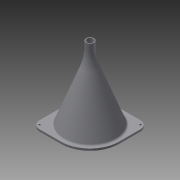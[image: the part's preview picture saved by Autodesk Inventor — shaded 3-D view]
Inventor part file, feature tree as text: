
AUTODESK INVENTOR PART (.ipt)
format: ipt  version: 2014 SP1 (Build 180222100, 222)  size: 177,152 bytes
history: native  units: in
note: dims shown in document units (in); Inventor stores cm internally (conversion verified against a paired STEP export)
features: sketch x5, extrude x4, other x1, plane x1, revolve x1
ambient origin geometry x8: Origin, YZ Plane, XZ Plane, XY Plane, X Axis, Y Axis, Z Axis, Center Point
bodies: Solid1 (feature_tree)
feature tree (12):
  extrude  "Extrusion1"  Depth=0.0787in
  extrude  "Extrusion2"  Depth=0.25in
  other  "Work Axis2"
  plane  "Work Plane5"
  revolve  "Revolution4"  [1 undecoded]
  extrude  "Extrusion6"  Depth=0.125in
  extrude  "Extrusion7"  TaperAngle=90.0deg  [1 undecoded]
  sketch  "Sketch1"  dims[d0=3.1496in d1=0.0787in]
  sketch  "Sketch2"  dims[d2=0.25in d3=0.0in d4=0.1969in]
  sketch  "Sketch10"  dims[d5=1.8505in d6=0.5in]
  sketch  "Sketch11"  dims[d7=0.125in d8=0.0in d40=0.125in]
  sketch  "Sketch12"  dims[d43=3.0in d53=90.0deg d54=90.0deg d59=1.25in d60=0.0741in d62=0.1165in d63=0.1165in d64=0.125in d65=0.0in d66=0.25in d67=0.0in]
note: 2 required parameter values undecoded (feature->parameter linkage not recoverable at this tier; creation-order binding heuristic only, values carry confidence <= 0.55)